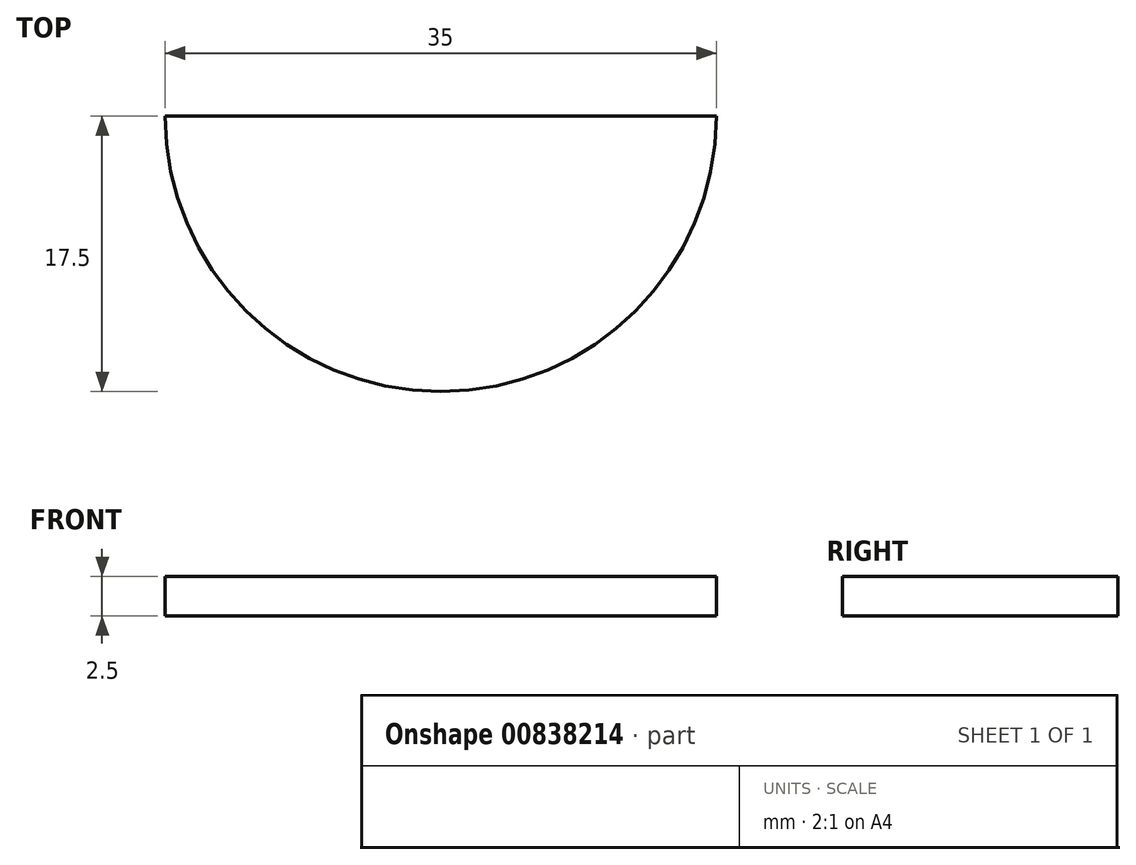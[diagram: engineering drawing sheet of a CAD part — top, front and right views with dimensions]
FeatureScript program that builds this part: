
annotation { "Feature Type Name" : "Feature", "Feature Type Description" : "" }
export const myFeature = defineFeature(function(context is Context, id is Id, definition is map)
    precondition{}
    {
        {
            var Q0;
            Q0=qCreatedBy(makeId("Top.planeOp"),FACE);
            var sketch = newSketch(context, id + "F0", { "sketchPlane" : qUnion([Q0])});
            skArc(sketch, "E0", {"start": v(-17.5, 0) * mm, "mid": v(0, -17.5) * mm, "end": v(17.5, 0) * mm});
            skLineSegment(sketch, "E1", {"start": v(-17.5, 0) * mm, "end": v(17.5, 0) * mm, "construction": true});
            skLineSegment(sketch, "E2", {"start": v(-17.5, 0) * mm, "end": v(17.5, 0) * mm});
            skPoint(sketch, "E3.orphan", {"position": v(-31.4, 0) * mm});
            skSolve(sketch);
        }
        {
            var Q0;
            Q0=qSketchRegion(id+"F0",true);
            extrude(context, id + "F1", {"entities" : qUnion([Q0]), "depth" : 2.5 * mm, "offsetDistance" : 25 * mm});
        }
    });
